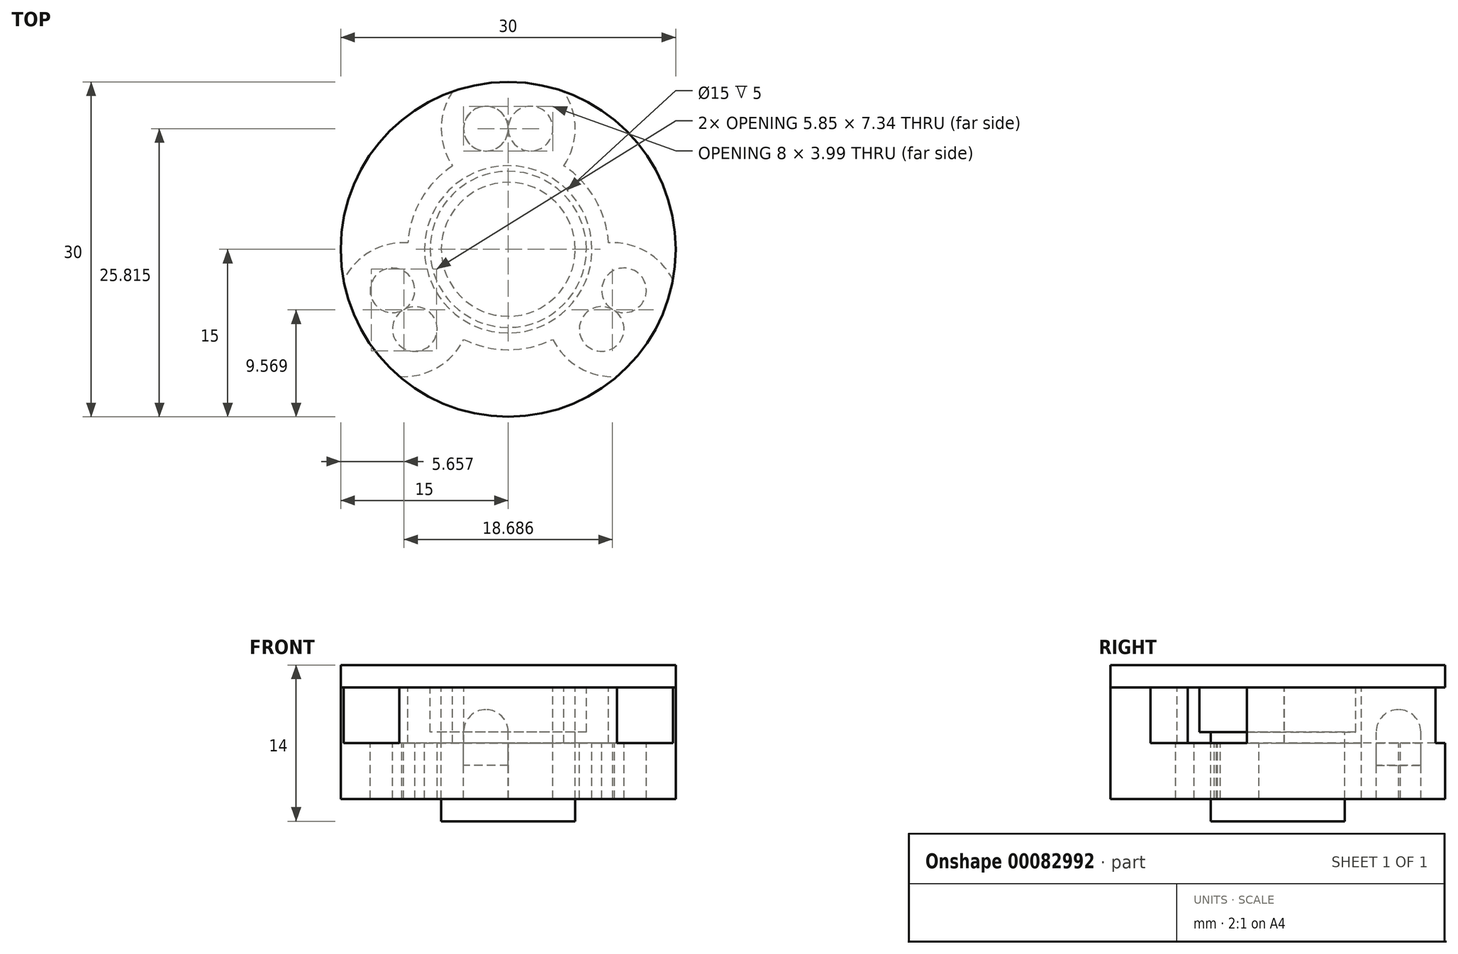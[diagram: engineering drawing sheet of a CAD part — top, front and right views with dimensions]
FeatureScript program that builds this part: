
annotation { "Feature Type Name" : "Feature", "Feature Type Description" : "" }
export const myFeature = defineFeature(function(context is Context, id is Id, definition is map)
    precondition{}
    {
        {
            var Q0;
            Q0=qCreatedBy(makeId("Top.planeOp"),FACE);
            var sketch = newSketch(context, id + "F0", { "sketchPlane" : qUnion([Q0])});
            skCircle(sketch, "E0", {"center": v(0, 0) * mm, "radius": 15 * mm});
            skCircle(sketch, "E1", {"center": v(0, 0) * mm, "radius": 7.5 * mm});
            skLineSegment(sketch, "E2", {"start": v(0, 0) * mm, "end": v(0, 25.16) * mm, "construction": true});
            skLineSegment(sketch, "E3", {"start": v(0, 0) * mm, "end": v(-21.76, -12.57) * mm, "construction": true});
            skLineSegment(sketch, "E4", {"start": v(21.03, -12.14) * mm, "end": v(0, 0) * mm, "construction": true});
            skCircle(sketch, "E5", {"center": v(0, 0) * mm, "radius": 11 * mm});
            skCircle(sketch, "E6", {"center": v(-2, 10.82) * mm, "radius": 2 * mm});
            skCircle(sketch, "E7.MirrorC", {"center": v(2, 10.82) * mm, "radius": 2 * mm});
            skCircle(sketch, "E8", {"center": v(-10.37, -3.68) * mm, "radius": 2 * mm});
            skCircle(sketch, "E9", {"center": v(-8.37, -7.14) * mm, "radius": 2 * mm});
            skCircle(sketch, "E10", {"center": v(10.37, -3.68) * mm, "radius": 2 * mm});
            skCircle(sketch, "E11", {"center": v(8.37, -7.14) * mm, "radius": 2 * mm});
            skCircle(sketch, "E12", {"center": v(0, 10.82) * mm, "radius": 6 * mm});
            skCircle(sketch, "E13", {"center": v(9.37, -5.4) * mm, "radius": 6 * mm});
            skCircle(sketch, "E14", {"center": v(-9.37, -5.4) * mm, "radius": 6 * mm});
            skSolve(sketch);
        }
        {
            var Q0;
            {var subQ0=sQuery(id+"F0.wireOp",EDGE,"E14");var subQ1=sQuery(id+"F0.wireOp",EDGE,"E0");var subQ2=makeQuery(id+"F0.imprint","INTERSECT",VERTEX,{"disambiguationData":[OD(1.0)],"derivedFrom":[subQ1,subQ0]});Q0=makeQuery(id+"F0.imprint","IMPRINT",FACE,{"disambiguationData":[TD([[makeQuery(id+"F0.imprint","IMPRINT",EDGE,{"disambiguationData":[TD([[subQ2,-1.0]])],"derivedFrom":subQ1}),1.0]])]});}
            var Q1;
            {var subQ5=sQuery(id+"F0.wireOp",EDGE,"E14");var subQ10=sQuery(id+"F0.wireOp",EDGE,"E0");var subQ11=makeQuery(id+"F0.imprint","INTERSECT",VERTEX,{"disambiguationData":[OD(0.0)],"derivedFrom":[subQ10,subQ5]});Q1=makeQuery(id+"F0.imprint","IMPRINT",FACE,{"disambiguationData":[TD([[makeQuery(id+"F0.imprint","IMPRINT",EDGE,{"disambiguationData":[TD([[subQ11,-1.0]])],"derivedFrom":subQ10}),1.0]])]});}
            var Q2;
            {var subQ0=sQuery(id+"F0.wireOp",EDGE,"E13");var subQ8=sQuery(id+"F0.wireOp",EDGE,"E0");var subQ11=makeQuery(id+"F0.imprint","INTERSECT",VERTEX,{"disambiguationData":[OD(0.0)],"derivedFrom":[subQ8,subQ0]});Q2=makeQuery(id+"F0.imprint","IMPRINT",FACE,{"disambiguationData":[TD([[makeQuery(id+"F0.imprint","IMPRINT",EDGE,{"disambiguationData":[TD([[subQ11,-1.0]])],"derivedFrom":subQ8}),1.0]])]});}
            var Q3;
            {var subQ0=sQuery(id+"F0.wireOp",EDGE,"E12");var subQ1=sQuery(id+"F0.wireOp",EDGE,"E0");var subQ2=makeQuery(id+"F0.imprint","INTERSECT",VERTEX,{"disambiguationData":[OD(1.0)],"derivedFrom":[subQ1,subQ0]});Q3=makeQuery(id+"F0.imprint","IMPRINT",FACE,{"disambiguationData":[TD([[makeQuery(id+"F0.imprint","IMPRINT",EDGE,{"disambiguationData":[TD([[subQ2,1.0]])],"derivedFrom":subQ1}),1.0]])]});}
            var Q4;
            {var subQ5=sQuery(id+"F0.wireOp",EDGE,"E12");var subQ6=sQuery(id+"F0.wireOp",EDGE,"E0");var subQ7=makeQuery(id+"F0.imprint","INTERSECT",VERTEX,{"disambiguationData":[OD(0.0)],"derivedFrom":[subQ6,subQ5]});Q4=makeQuery(id+"F0.imprint","IMPRINT",FACE,{"disambiguationData":[TD([[makeQuery(id+"F0.imprint","IMPRINT",EDGE,{"disambiguationData":[TD([[subQ7,1.0]])],"derivedFrom":subQ6}),1.0]])]});}
            var Q5;
            {var subQ0=sQuery(id+"F0.wireOp",EDGE,"E12");var subQ1=sQuery(id+"F0.wireOp",EDGE,"E0");var subQ2=makeQuery(id+"F0.imprint","INTERSECT",VERTEX,{"disambiguationData":[OD(0.0)],"derivedFrom":[subQ1,subQ0]});Q5=makeQuery(id+"F0.imprint","IMPRINT",FACE,{"disambiguationData":[TD([[makeQuery(id+"F0.imprint","IMPRINT",EDGE,{"disambiguationData":[TD([[subQ2,-1.0]])],"derivedFrom":subQ1}),1.0]])]});}
            var Q6;
            {var subQ0=sQuery(id+"F0.wireOp",EDGE,"E14");var subQ1=sQuery(id+"F0.wireOp",EDGE,"E1");var subQ2=makeQuery(id+"F0.imprint","INTERSECT",VERTEX,{"disambiguationData":[OD(1.0)],"derivedFrom":[subQ1,subQ0]});Q6=makeQuery(id+"F0.imprint","IMPRINT",FACE,{"disambiguationData":[TD([[makeQuery(id+"F0.imprint","IMPRINT",EDGE,{"disambiguationData":[TD([[subQ2,-1.0]])],"derivedFrom":subQ1}),-1.0]])]});}
            var Q7;
            {var subQ0=sQuery(id+"F0.wireOp",EDGE,"E12");var subQ1=sQuery(id+"F0.wireOp",EDGE,"E1");var subQ2=makeQuery(id+"F0.imprint","INTERSECT",VERTEX,{"disambiguationData":[OD(0.0)],"derivedFrom":[subQ1,subQ0]});Q7=makeQuery(id+"F0.imprint","IMPRINT",FACE,{"disambiguationData":[TD([[makeQuery(id+"F0.imprint","IMPRINT",EDGE,{"disambiguationData":[TD([[subQ2,1.0]])],"derivedFrom":subQ1}),-1.0]])]});}
            var Q8;
            {var subQ0=sQuery(id+"F0.wireOp",EDGE,"E12");var subQ1=sQuery(id+"F0.wireOp",EDGE,"E1");var subQ2=makeQuery(id+"F0.imprint","INTERSECT",VERTEX,{"disambiguationData":[OD(1.0)],"derivedFrom":[subQ1,subQ0]});Q8=makeQuery(id+"F0.imprint","IMPRINT",FACE,{"disambiguationData":[TD([[makeQuery(id+"F0.imprint","IMPRINT",EDGE,{"disambiguationData":[TD([[subQ2,-1.0]])],"derivedFrom":subQ1}),-1.0]])]});}
            var Q9;
            {var subQ5=sQuery(id+"F0.wireOp",EDGE,"E12");var subQ6=sQuery(id+"F0.wireOp",EDGE,"E1");var subQ7=makeQuery(id+"F0.imprint","INTERSECT",VERTEX,{"disambiguationData":[OD(0.0)],"derivedFrom":[subQ6,subQ5]});Q9=makeQuery(id+"F0.imprint","IMPRINT",FACE,{"disambiguationData":[TD([[makeQuery(id+"F0.imprint","IMPRINT",EDGE,{"disambiguationData":[TD([[subQ7,-1.0]])],"derivedFrom":subQ6}),-1.0]])]});}
            var Q10;
            {var subQ5=sQuery(id+"F0.wireOp",EDGE,"E13");var subQ9=sQuery(id+"F0.wireOp",EDGE,"E1");var subQ10=makeQuery(id+"F0.imprint","INTERSECT",VERTEX,{"disambiguationData":[OD(0.0)],"derivedFrom":[subQ9,subQ5]});Q10=makeQuery(id+"F0.imprint","IMPRINT",FACE,{"disambiguationData":[TD([[makeQuery(id+"F0.imprint","IMPRINT",EDGE,{"disambiguationData":[TD([[subQ10,1.0]])],"derivedFrom":subQ9}),-1.0]])]});}
            var Q11;
            {var subQ6=sQuery(id+"F0.wireOp",EDGE,"E14");var subQ8=sQuery(id+"F0.wireOp",EDGE,"E1");var subQ9=makeQuery(id+"F0.imprint","INTERSECT",VERTEX,{"disambiguationData":[OD(0.0)],"derivedFrom":[subQ8,subQ6]});Q11=makeQuery(id+"F0.imprint","IMPRINT",FACE,{"disambiguationData":[TD([[makeQuery(id+"F0.imprint","IMPRINT",EDGE,{"disambiguationData":[TD([[subQ9,-1.0]])],"derivedFrom":subQ8}),-1.0]])]});}
            extrude(context, id + "F1", {"entities" : qUnion([Q0, Q1, Q2, Q3, Q4, Q5, Q6, Q7, Q8, Q9, Q10, Q11]), "oppositeDirection" : true, "depth" : 10 * mm});
        }
        {
            var Q0;
            {var subQ5=sQuery(id+"F0.wireOp",EDGE,"E12");var subQ6=sQuery(id+"F0.wireOp",EDGE,"E1");var subQ7=makeQuery(id+"F0.imprint","INTERSECT",VERTEX,{"disambiguationData":[OD(0.0)],"derivedFrom":[subQ6,subQ5]});Q0=makeQuery(id+"F0.imprint","IMPRINT",FACE,{"disambiguationData":[TD([[makeQuery(id+"F0.imprint","IMPRINT",EDGE,{"disambiguationData":[TD([[subQ7,-1.0]])],"derivedFrom":subQ6}),-1.0]])]});}
            var Q1;
            {var subQ5=sQuery(id+"F0.wireOp",EDGE,"E12");var subQ6=sQuery(id+"F0.wireOp",EDGE,"E0");var subQ7=makeQuery(id+"F0.imprint","INTERSECT",VERTEX,{"disambiguationData":[OD(0.0)],"derivedFrom":[subQ6,subQ5]});Q1=makeQuery(id+"F0.imprint","IMPRINT",FACE,{"disambiguationData":[TD([[makeQuery(id+"F0.imprint","IMPRINT",EDGE,{"disambiguationData":[TD([[subQ7,1.0]])],"derivedFrom":subQ6}),1.0]])]});}
            var Q2;
            {var subQ6=sQuery(id+"F0.wireOp",EDGE,"E14");var subQ8=sQuery(id+"F0.wireOp",EDGE,"E1");var subQ9=makeQuery(id+"F0.imprint","INTERSECT",VERTEX,{"disambiguationData":[OD(0.0)],"derivedFrom":[subQ8,subQ6]});Q2=makeQuery(id+"F0.imprint","IMPRINT",FACE,{"disambiguationData":[TD([[makeQuery(id+"F0.imprint","IMPRINT",EDGE,{"disambiguationData":[TD([[subQ9,-1.0]])],"derivedFrom":subQ8}),-1.0]])]});}
            var Q3;
            {var subQ5=sQuery(id+"F0.wireOp",EDGE,"E14");var subQ10=sQuery(id+"F0.wireOp",EDGE,"E0");var subQ11=makeQuery(id+"F0.imprint","INTERSECT",VERTEX,{"disambiguationData":[OD(0.0)],"derivedFrom":[subQ10,subQ5]});Q3=makeQuery(id+"F0.imprint","IMPRINT",FACE,{"disambiguationData":[TD([[makeQuery(id+"F0.imprint","IMPRINT",EDGE,{"disambiguationData":[TD([[subQ11,-1.0]])],"derivedFrom":subQ10}),1.0]])]});}
            var Q4;
            {var subQ5=sQuery(id+"F0.wireOp",EDGE,"E13");var subQ9=sQuery(id+"F0.wireOp",EDGE,"E1");var subQ10=makeQuery(id+"F0.imprint","INTERSECT",VERTEX,{"disambiguationData":[OD(0.0)],"derivedFrom":[subQ9,subQ5]});Q4=makeQuery(id+"F0.imprint","IMPRINT",FACE,{"disambiguationData":[TD([[makeQuery(id+"F0.imprint","IMPRINT",EDGE,{"disambiguationData":[TD([[subQ10,1.0]])],"derivedFrom":subQ9}),-1.0]])]});}
            var Q5;
            {var subQ0=sQuery(id+"F0.wireOp",EDGE,"E13");var subQ8=sQuery(id+"F0.wireOp",EDGE,"E0");var subQ11=makeQuery(id+"F0.imprint","INTERSECT",VERTEX,{"disambiguationData":[OD(0.0)],"derivedFrom":[subQ8,subQ0]});Q5=makeQuery(id+"F0.imprint","IMPRINT",FACE,{"disambiguationData":[TD([[makeQuery(id+"F0.imprint","IMPRINT",EDGE,{"disambiguationData":[TD([[subQ11,-1.0]])],"derivedFrom":subQ8}),1.0]])]});}
            extrude(context, id + "F2", {"entities" : qUnion([Q0, Q1, Q2, Q3, Q4, Q5]), "operationType" : NewBodyOperationType.REMOVE, "oppositeDirection" : true, "depth" : 5 * mm});
        }
        {
            var Q0;
            {var subQ1=sQuery(id+"F0.wireOp",EDGE,"E1");var subQ5=sQuery(id+"F0.wireOp",EDGE,"E12");var subQ8=makeQuery(id+"F0.imprint","INTERSECT",VERTEX,{"disambiguationData":[OD(0.0)],"derivedFrom":[subQ1,subQ5]});Q0=makeQuery(id+"F0.imprint","IMPRINT",FACE,{"disambiguationData":[TD([[makeQuery(id+"F0.imprint","IMPRINT",EDGE,{"disambiguationData":[TD([[subQ8,1.0]])],"derivedFrom":subQ1}),1.0]])]});}
            var sketch = newSketch(context, id + "F3", { "sketchPlane" : qUnion([Q0])});
            skCircle(sketch, "E15.0", {"center": v(0, 0) * mm, "radius": 15 * mm});
            skSolve(sketch);
        }
        {
            var Q0;
            Q0 = qSketchRegion(id + "F3", true);
            extrude(context, id + "F4", {"entities" : qUnion([Q0]), "depth" : 2 * mm});
        }
        {
            var Q0;
            Q0=qCreatedBy(makeId("Top.planeOp"),FACE);
            var sketch = newSketch(context, id + "F5", { "sketchPlane" : qUnion([Q0])});
            skCircle(sketch, "E16", {"center": v(0, 0) * mm, "radius": 6 * mm});
            skCircle(sketch, "E17", {"center": v(0, 0) * mm, "radius": 7 * mm});
            skCircle(sketch, "E18", {"center": v(0, 0) * mm, "radius": 9 * mm});
            skSolve(sketch);
        }
        {
            var Q0;
            Q0=makeQuery(id+"F5.imprint","IMPRINT",FACE,{"disambiguationData":[TD([[makeQuery(id+"F5.imprint","IMPRINT",EDGE,{"derivedFrom":sQuery(id+"F5.wireOp",EDGE,"E16")}),1.0]])]});
            extrude(context, id + "F6", {"entities" : qUnion([Q0]), "oppositeDirection" : true, "depth" : 12 * mm});
        }
        {
            var Q0;
            Q0=makeQuery(id+"F5.imprint","IMPRINT",FACE,{"disambiguationData":[TD([[makeQuery(id+"F5.imprint","IMPRINT",EDGE,{"derivedFrom":sQuery(id+"F5.wireOp",EDGE,"E16")}),-1.0]])]});
            var Q1;
            Q1=makeQuery(id+"F5.imprint","IMPRINT",FACE,{"disambiguationData":[TD([[makeQuery(id+"F5.imprint","IMPRINT",EDGE,{"derivedFrom":sQuery(id+"F5.wireOp",EDGE,"E16")}),1.0]])]});
            extrude(context, id + "F7", {"entities" : qUnion([Q0, Q1]), "operationType" : NewBodyOperationType.ADD, "oppositeDirection" : true, "depth" : 4 * mm});
        }
        {
            var Q0;
            Q0=makeQuery(id+"F5.imprint","IMPRINT",FACE,{"disambiguationData":[TD([[makeQuery(id+"F5.imprint","IMPRINT",EDGE,{"derivedFrom":sQuery(id+"F5.wireOp",EDGE,"E17")}),-1.0]])]});
            extrude(context, id + "F8", {"entities" : qUnion([Q0]), "operationType" : NewBodyOperationType.REMOVE, "oppositeDirection" : true, "depth" : 5 * mm});
        }
        {
            var Q0;
            {var subQ0=sQuery(id+"F0.wireOp",EDGE,"E6");var subQ1=sQuery(id+"F0.wireOp",EDGE,"E5");var subQ2=makeQuery(id+"F0.imprint","INTERSECT",VERTEX,{"disambiguationData":[OD(0.0)],"derivedFrom":[subQ1,subQ0]});Q0=makeQuery(id+"F0.imprint","IMPRINT",FACE,{"disambiguationData":[TD([[makeQuery(id+"F0.imprint","IMPRINT",EDGE,{"disambiguationData":[TD([[subQ2,-1.0]])],"derivedFrom":subQ1}),1.0]])]});}
            var Q1;
            {var subQ0=sQuery(id+"F0.wireOp",EDGE,"E6");var subQ1=sQuery(id+"F0.wireOp",EDGE,"E5");var subQ2=makeQuery(id+"F0.imprint","INTERSECT",VERTEX,{"disambiguationData":[OD(0.0)],"derivedFrom":[subQ1,subQ0]});Q1=makeQuery(id+"F0.imprint","IMPRINT",FACE,{"disambiguationData":[TD([[makeQuery(id+"F0.imprint","IMPRINT",EDGE,{"disambiguationData":[TD([[subQ2,-1.0]])],"derivedFrom":subQ1}),-1.0]])]});}
            extrude(context, id + "F9", {"entities" : qUnion([Q0, Q1]), "oppositeDirection" : true, "depth" : 5 * mm});
        }
        {
            var Q0;
            Q0=makeQuery(id+"F9.opExtrude","CAP_FACE",FACE,{"disambiguationData":[OSD([sQuery(id+"F0.wireOp",EDGE,"E6")])],"isStart":true});
            fillet(context, id + "F10", {"entities" : qUnion([Q0]), "radius" : 2 * mm, "tangentPropagation" : true, "allowEdgeOverflow" : false});
        }
        {
            var Q0;
            Q0=makeQuery(id+"F9.opExtrude","SWEPT_BODY",BODY,{"disambiguationData":[OSD([sQuery(id+"F0.wireOp",EDGE,"E6")])]});
            transform(context, id + "F11", {"entities" : qUnion([Q0]), "transformType" : TransformType.TRANSLATION_3D, "dx" : 0 * mm, "dy" : 0 * mm, "dz" : -2 * mm, "makeCopy" : false});
        }
    });
